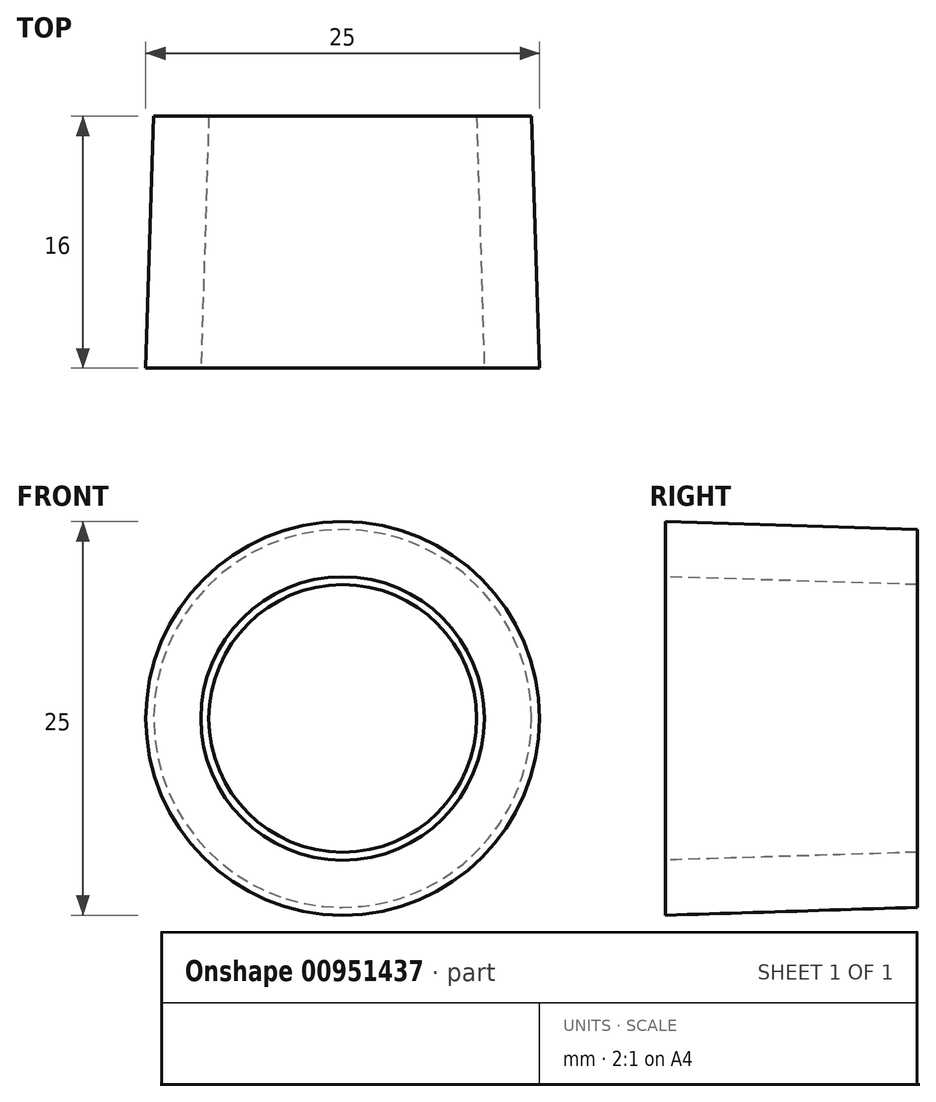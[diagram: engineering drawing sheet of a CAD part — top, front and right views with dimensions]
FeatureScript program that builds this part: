
annotation { "Feature Type Name" : "Feature", "Feature Type Description" : "" }
export const myFeature = defineFeature(function(context is Context, id is Id, definition is map)
    precondition{}
    {
        {
            var Q0;
            Q0=qCreatedBy(makeId("Top.planeOp"),FACE);
            var sketch = newSketch(context, id + "F0", { "sketchPlane" : qUnion([Q0])});
            skLineSegment(sketch, "E0", {"start": v(-9, 0) * mm, "end": v(-8.5, 16) * mm});
            skLineSegment(sketch, "E1", {"start": v(-8.5, 16) * mm, "end": v(-12, 16) * mm});
            skLineSegment(sketch, "E2", {"start": v(-12, 16) * mm, "end": v(-12.5, 0) * mm});
            skLineSegment(sketch, "E3", {"start": v(-12.5, 0) * mm, "end": v(-9, 0) * mm});
            skLineSegment(sketch, "E4", {"start": v(0, 0) * mm, "end": v(0, 34.47) * mm, "construction": true});
            skSolve(sketch);
        }
        {
            var Q0;
            Q0 = qSketchRegion(id + "F0", true);
            var Q1;
            Q1=sQuery(id+"F0.wireOp",EDGE,"E4");
            revolve(context, id + "F1", {"surfaceOperationType" : NewSurfaceOperationType.NEW, "entities" : qUnion([Q0]), "axis" : qUnion([Q1]), "revolveType" : RevolveType.FULL});
        }
    });
